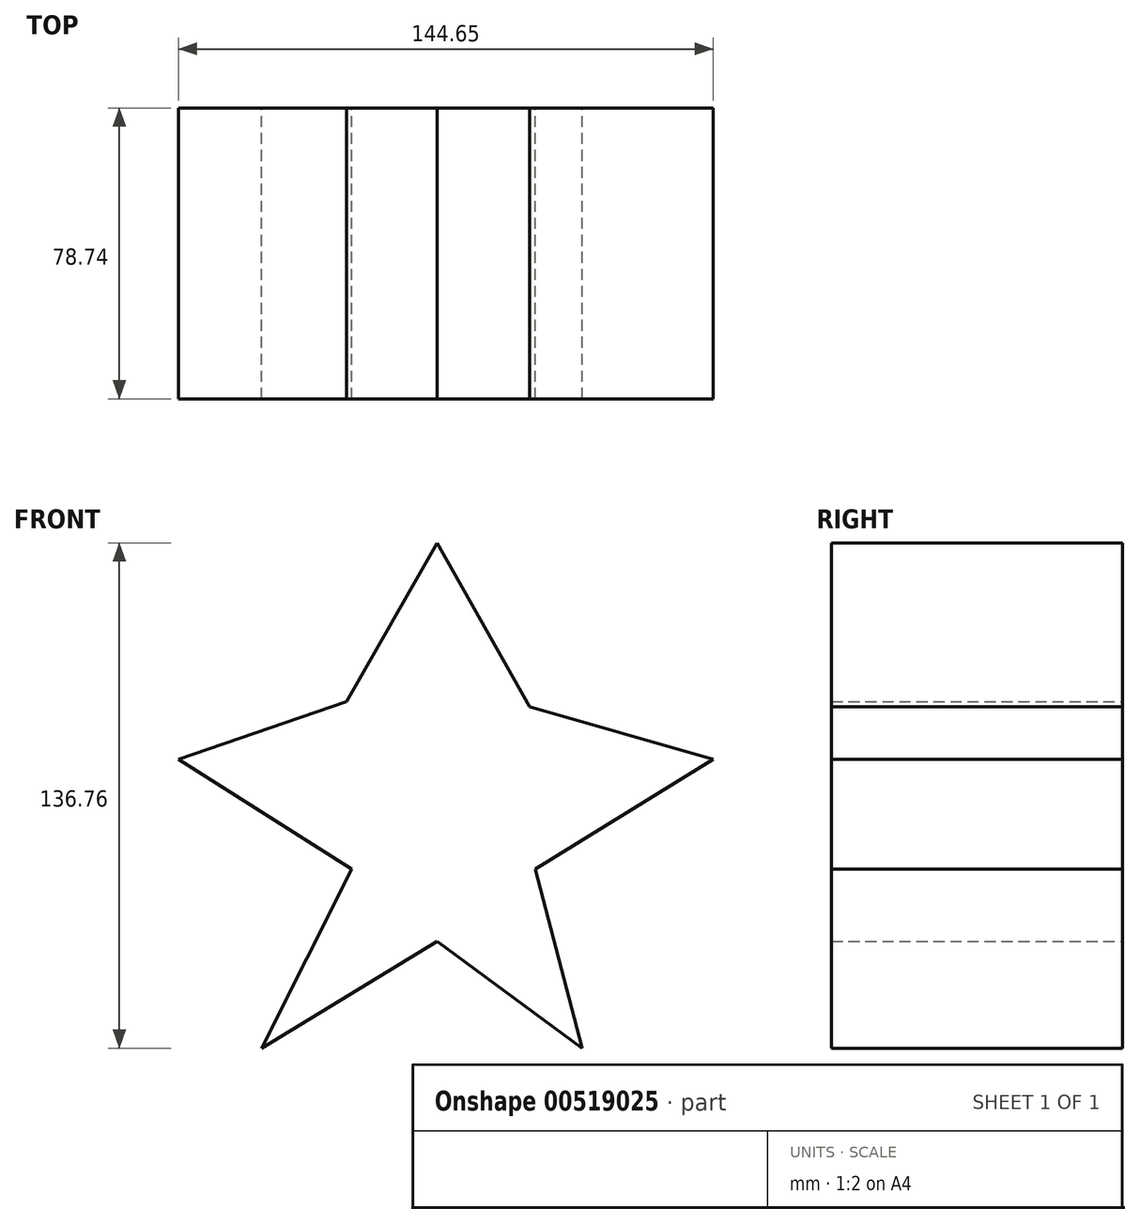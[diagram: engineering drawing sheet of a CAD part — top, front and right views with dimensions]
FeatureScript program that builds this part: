
annotation { "Feature Type Name" : "Feature", "Feature Type Description" : "" }
export const myFeature = defineFeature(function(context is Context, id is Id, definition is map)
    precondition{}
    {
        {
            var Q0;
            Q0=qCreatedBy(makeId("Front.planeOp"),FACE);
            var sketch = newSketch(context, id + "F0", { "sketchPlane" : qUnion([Q0])});
            skLineSegment(sketch, "E0", {"start": v(0, 65.82) * mm, "end": v(-24.44, 22.86) * mm});
            skLineSegment(sketch, "E1", {"start": v(-24.44, 22.86) * mm, "end": v(-69.96, 7.3) * mm});
            skLineSegment(sketch, "E2", {"start": v(-69.96, 7.3) * mm, "end": v(-23.06, -22.47) * mm});
            skLineSegment(sketch, "E3", {"start": v(-23.06, -22.47) * mm, "end": v(-47.5, -70.94) * mm});
            skLineSegment(sketch, "E4", {"start": v(-47.5, -70.94) * mm, "end": v(0, -41.98) * mm});
            skLineSegment(sketch, "E5", {"start": v(0, -41.98) * mm, "end": v(39.22, -70.94) * mm});
            skLineSegment(sketch, "E6", {"start": v(39.22, -70.94) * mm, "end": v(26.6, -22.47) * mm});
            skLineSegment(sketch, "E7", {"start": v(26.6, -22.47) * mm, "end": v(74.69, 7.3) * mm});
            skLineSegment(sketch, "E8", {"start": v(74.69, 7.3) * mm, "end": v(25.05, 21.49) * mm});
            skLineSegment(sketch, "E9", {"start": v(25.05, 21.49) * mm, "end": v(0, 65.82) * mm});
            skSolve(sketch);
        }
        {
            var Q0;
            Q0=makeQuery(id+"F0.imprint","IMPRINT",FACE,{"disambiguationData":[TD([[makeQuery(id+"F0.imprint","IMPRINT",EDGE,{"derivedFrom":sQuery(id+"F0.wireOp",EDGE,"E0")}),1.0]])]});
            extrude(context, id + "F1", {"entities" : qUnion([Q0]), "endBound" : BoundingType.SYMMETRIC, "depth" : 78.74 * mm, "offsetDistance" : 25.4 * mm});
        }
    });
